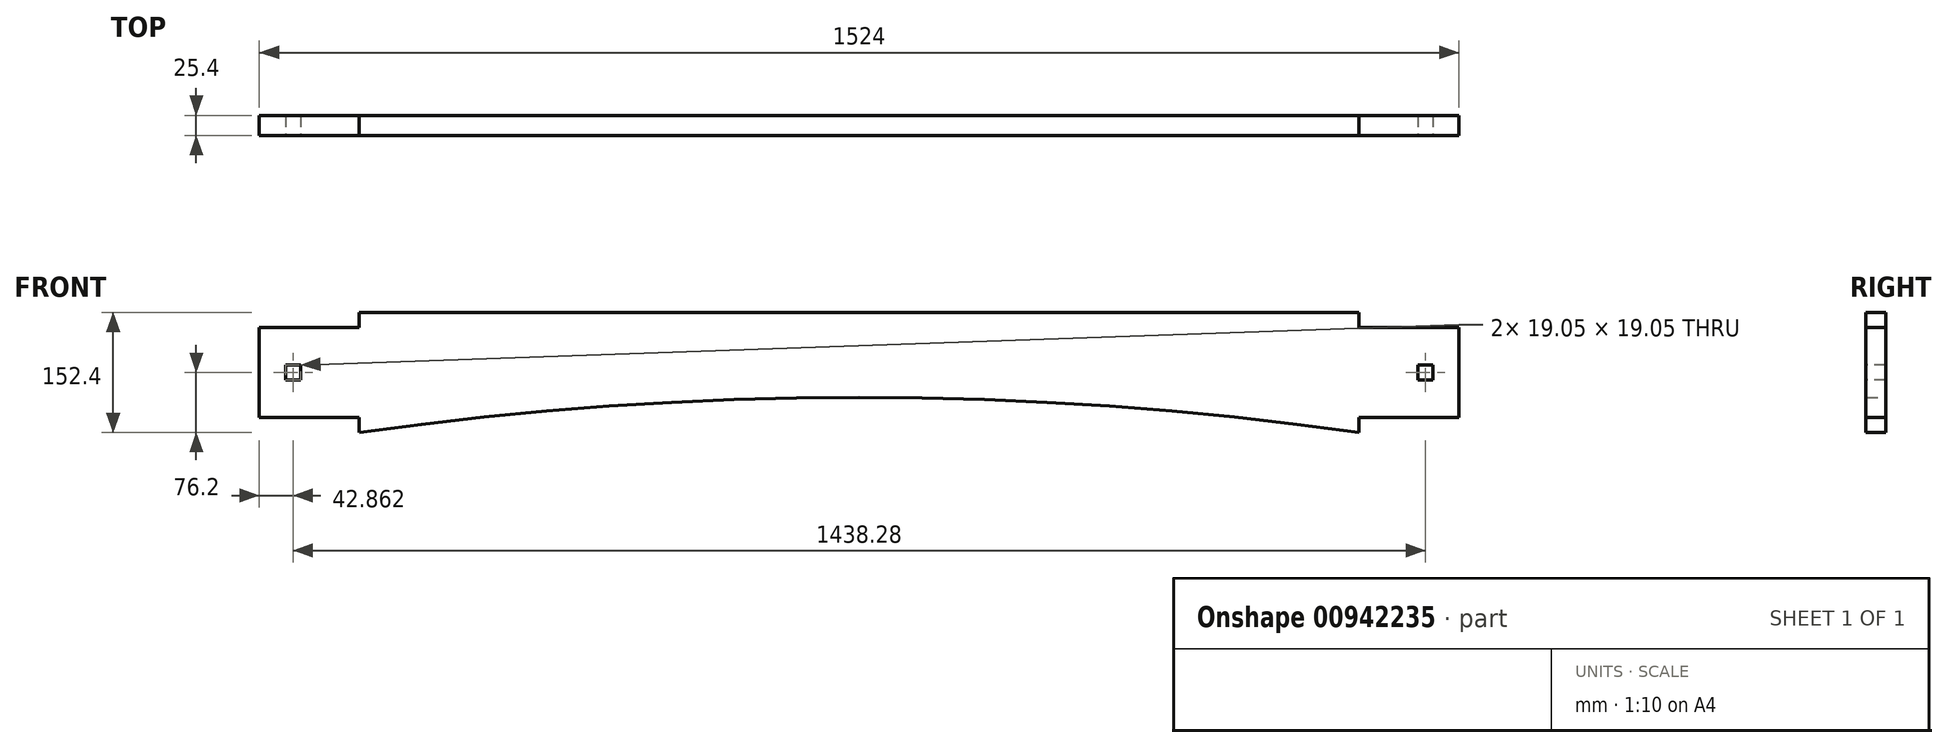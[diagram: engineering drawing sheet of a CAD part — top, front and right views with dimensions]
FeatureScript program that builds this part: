
annotation { "Feature Type Name" : "Feature", "Feature Type Description" : "" }
export const myFeature = defineFeature(function(context is Context, id is Id, definition is map)
    precondition{}
    {
        {
            var Q0;
            Q0=qCreatedBy(makeId("Front.planeOp"),FACE);
            var sketch = newSketch(context, id + "F0", { "sketchPlane" : qUnion([Q0])});
            skLineSegment(sketch, "E0.bottom", {"start": v(635, 76.2) * mm, "end": v(-635, 76.2) * mm});
            skLineSegment(sketch, "E0.left", {"start": v(635, 76.2) * mm, "end": v(635, -76.2) * mm});
            skLineSegment(sketch, "E0.right", {"start": v(-635, 76.2) * mm, "end": v(-635, -76.2) * mm});
            skPoint(sketch, "E0.middle", {"position": v(0, 0) * mm});
            skPoint(sketch, "E0.top.end.orphan", {"position": v(0, -76.2) * mm});
            skArc(sketch, "E1", {"start": v(635, -76.2) * mm, "mid": v(0, -31.75) * mm, "end": v(-635, -76.2) * mm});
            skSolve(sketch);
        }
        {
            var Q0;
            Q0 = qSketchRegion(id + "F0", true);
            extrude(context, id + "F1", {"entities" : qUnion([Q0]), "depth" : 25.4 * mm, "offsetDistance" : 25.4 * mm});
        }
        {
            var Q0;
            Q0=makeQuery(id+"F1.opExtrude","SWEPT_FACE",FACE,{"disambiguationData":[OSD([sQuery(id+"F0.wireOp",EDGE,"E0.right")])]});
            var sketch = newSketch(context, id + "F2", { "sketchPlane" : qUnion([Q0])});
            skLineSegment(sketch, "E2.bottom", {"start": v(25.4, 57.15) * mm, "end": v(0, 57.15) * mm});
            skLineSegment(sketch, "E2.top", {"start": v(25.4, -57.15) * mm, "end": v(0, -57.15) * mm});
            skLineSegment(sketch, "E2.left", {"start": v(25.4, 57.15) * mm, "end": v(25.4, -57.15) * mm});
            skPoint(sketch, "E2.middle", {"position": v(0, 0) * mm});
            skLineSegment(sketch, "E3", {"start": v(0, 57.15) * mm, "end": v(0, -57.15) * mm});
            skPoint(sketch, "E2.right.start.orphan", {"position": v(-25.4, 57.15) * mm});
            skPoint(sketch, "E4.orphan", {"position": v(-25.4, -57.15) * mm});
            skSolve(sketch);
        }
        {
            var Q0;
            Q0 = qSketchRegion(id + "F2", true);
            extrude(context, id + "F3", {"entities" : qUnion([Q0]), "operationType" : NewBodyOperationType.ADD, "depth" : 127 * mm, "offsetDistance" : 25.4 * mm});
        }
        {
            var Q0;
            Q0=makeQuery(id+"F1.opExtrude","SWEPT_FACE",FACE,{"disambiguationData":[OSD([sQuery(id+"F0.wireOp",EDGE,"E0.left")])]});
            var sketch = newSketch(context, id + "F4", { "sketchPlane" : qUnion([Q0])});
            skLineSegment(sketch, "E5.bottom", {"start": v(-25.4, 57.15) * mm, "end": v(0, 57.15) * mm});
            skLineSegment(sketch, "E5.top", {"start": v(-25.4, -57.15) * mm, "end": v(0, -57.15) * mm});
            skLineSegment(sketch, "E5.left", {"start": v(-25.4, 57.15) * mm, "end": v(-25.4, -57.15) * mm});
            skPoint(sketch, "E5.middle", {"position": v(0, 0) * mm});
            skLineSegment(sketch, "E6", {"start": v(0, 57.15) * mm, "end": v(0, -57.15) * mm});
            skPoint(sketch, "E5.right.start.orphan", {"position": v(25.4, 57.15) * mm});
            skPoint(sketch, "E7.orphan", {"position": v(25.4, -57.15) * mm});
            skSolve(sketch);
        }
        {
            var Q0;
            Q0 = qSketchRegion(id + "F4", true);
            extrude(context, id + "F5", {"entities" : qUnion([Q0]), "operationType" : NewBodyOperationType.ADD, "depth" : 127 * mm, "offsetDistance" : 25.4 * mm});
        }
        {
            var Q0;
            Q0=makeQuery(id+"F5.boolean.opBoolean","MERGE",FACE,{"derivedFrom":[makeQuery(id+"F3.boolean.opBoolean","MERGE",FACE,{"derivedFrom":[makeQuery(id+"F1.opExtrude","CAP_FACE",FACE,{"disambiguationData":[OSD([sQuery(id+"F0.wireOp",EDGE,"E0.bottom"),sQuery(id+"F0.wireOp",EDGE,"E0.left"),sQuery(id+"F0.wireOp",EDGE,"E0.right"),sQuery(id+"F0.wireOp",EDGE,"qREkz5Ee-QOWv-B1bH-gHnn-l1VKZGbg5kAc")])],"isStart":false}),makeQuery(id+"F3.opExtrude","SWEPT_FACE",FACE,{"disambiguationData":[OSD([sQuery(id+"F2.wireOp",EDGE,"E2.left")])]})]}),makeQuery(id+"F5.opExtrude","SWEPT_FACE",FACE,{"disambiguationData":[OSD([sQuery(id+"F4.wireOp",EDGE,"E5.left")])]})]});
            var sketch = newSketch(context, id + "F6", { "sketchPlane" : qUnion([Q0])});
            skLineSegment(sketch, "E8", {"start": v(-762, 57.15) * mm, "end": v(-709.61, 57.15) * mm});
            skLineSegment(sketch, "E9", {"start": v(-709.61, 9.52) * mm, "end": v(-709.61, -9.53) * mm});
            skLineSegment(sketch, "E10.bottom", {"start": v(-728.66, 9.52) * mm, "end": v(-709.61, 9.52) * mm});
            skLineSegment(sketch, "E10.top", {"start": v(-728.66, -9.53) * mm, "end": v(-709.61, -9.53) * mm});
            skLineSegment(sketch, "E10.left", {"start": v(-728.66, 9.52) * mm, "end": v(-728.66, -9.53) * mm});
            skPoint(sketch, "E10.middle", {"position": v(-709.61, 0) * mm});
            skPoint(sketch, "E10.right.start.orphan", {"position": v(-690.56, 9.52) * mm});
            skPoint(sketch, "E11.orphan", {"position": v(-690.56, -9.53) * mm});
            skPoint(sketch, "E12.orphan", {"position": v(-709.61, -57.15) * mm});
            skLineSegment(sketch, "E13.MirrorCS", {"start": v(728.66, 9.52) * mm, "end": v(709.61, 9.52) * mm});
            skLineSegment(sketch, "E14.MirrorCS", {"start": v(728.66, 9.52) * mm, "end": v(728.66, -9.53) * mm});
            skLineSegment(sketch, "E15.MirrorCS", {"start": v(728.66, -9.53) * mm, "end": v(709.61, -9.53) * mm});
            skLineSegment(sketch, "E16.MirrorCS", {"start": v(709.61, 9.52) * mm, "end": v(709.61, -9.53) * mm});
            skSolve(sketch);
        }
        {
            var Q0;
            Q0 = qSketchRegion(id + "F6", true);
            extrude(context, id + "F7", {"entities" : qUnion([Q0]), "operationType" : NewBodyOperationType.REMOVE, "endBound" : BoundingType.THROUGH_ALL, "oppositeDirection" : true, "depth" : 25.4 * mm, "offsetDistance" : 25.4 * mm});
        }
    });
